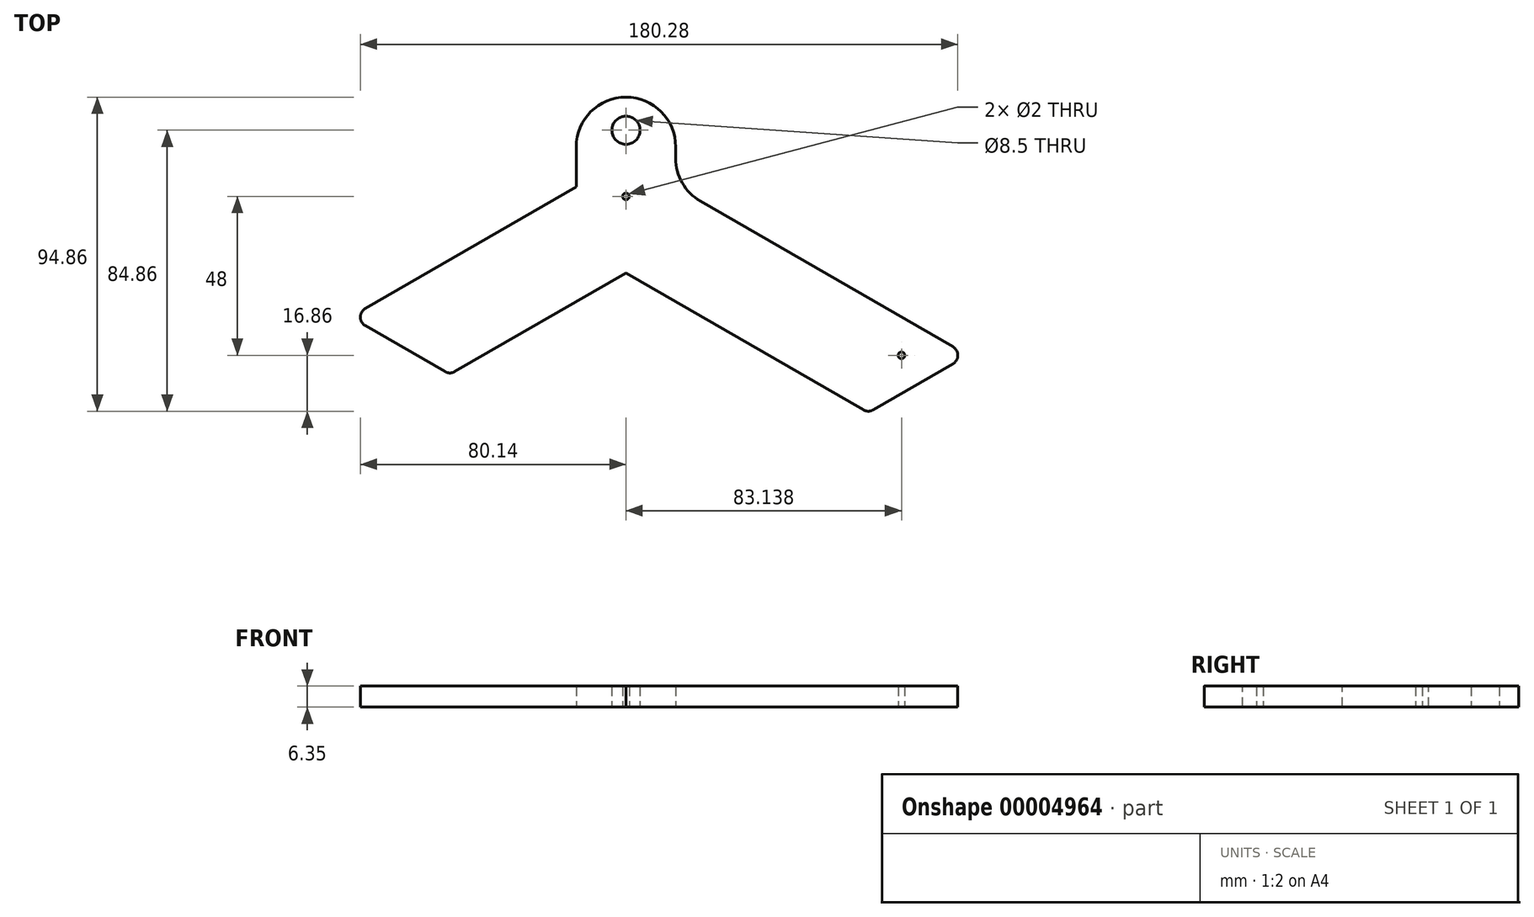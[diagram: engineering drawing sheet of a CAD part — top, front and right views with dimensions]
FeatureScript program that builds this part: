
annotation { "Feature Type Name" : "Feature", "Feature Type Description" : "" }
export const myFeature = defineFeature(function(context is Context, id is Id, definition is map)
    precondition{}
    {
        {
            var Q0;
            Q0=qCreatedBy(makeId("Top.planeOp"),FACE);
            var sketch = newSketch(context, id + "F0", { "sketchPlane" : qUnion([Q0])});
            skLineSegment(sketch, "E0", {"start": v(0, 0) * mm, "end": v(0, 96) * mm, "construction": true});
            skLineSegment(sketch, "E1", {"start": v(0, 96) * mm, "end": v(83.14, 48) * mm, "construction": true});
            skLineSegment(sketch, "E2", {"start": v(83.14, 48) * mm, "end": v(0, 0) * mm, "construction": true});
            skCircle(sketch, "E3", {"center": v(0, 96) * mm, "radius": 1 * mm});
            skCircle(sketch, "E4", {"center": v(83.14, 48) * mm, "radius": 1 * mm});
            skLineSegment(sketch, "E5", {"start": v(0, 96) * mm, "end": v(0, 116) * mm, "construction": true});
            skCircle(sketch, "E6", {"center": v(0, 116) * mm, "radius": 4.25 * mm});
            skLineSegment(sketch, "E7", {"start": v(-15, 81.57) * mm, "end": v(73.14, 30.68) * mm});
            skLineSegment(sketch, "E8", {"start": v(73.14, 30.68) * mm, "end": v(103.14, 48) * mm});
            skLineSegment(sketch, "E9", {"start": v(103.14, 48) * mm, "end": v(15, 98.89) * mm});
            skLineSegment(sketch, "E10", {"start": v(-15, 81.57) * mm, "end": v(-15, 126) * mm});
            skLineSegment(sketch, "E11", {"start": v(15, 98.89) * mm, "end": v(15, 126) * mm});
            skLineSegment(sketch, "E12", {"start": v(15, 126) * mm, "end": v(-15, 126) * mm});
            skLineSegment(sketch, "E13", {"start": v(0, 116) * mm, "end": v(0, 126) * mm, "construction": true});
            skLineSegment(sketch, "E14.1.0", {"start": v(-116.62, -50) * mm, "end": v(-101.62, -76) * mm, "construction": true});
            skLineSegment(sketch, "E14.1.1", {"start": v(-63.14, -53.77) * mm, "end": v(-101.62, -76) * mm, "construction": true});
            skLineSegment(sketch, "E14.1.2", {"start": v(-93.14, -36.45) * mm, "end": v(-116.62, -50) * mm, "construction": true});
            skLineSegment(sketch, "E14.1.3", {"start": v(-93.14, 65.32) * mm, "end": v(-93.14, -36.45) * mm, "construction": true});
            skLineSegment(sketch, "E14.1.4", {"start": v(-63.14, 48) * mm, "end": v(-93.14, 65.32) * mm, "construction": true});
            skLineSegment(sketch, "E14.1.5", {"start": v(-63.14, -53.77) * mm, "end": v(-63.14, 48) * mm, "construction": true});
            skLineSegment(sketch, "E14.2.0", {"start": v(101.62, -76) * mm, "end": v(116.62, -50) * mm, "construction": true});
            skLineSegment(sketch, "E14.2.1", {"start": v(78.14, -27.8) * mm, "end": v(116.62, -50) * mm, "construction": true});
            skLineSegment(sketch, "E14.2.2", {"start": v(78.14, -62.43) * mm, "end": v(101.62, -76) * mm, "construction": true});
            skLineSegment(sketch, "E14.2.3", {"start": v(-10, -113.32) * mm, "end": v(78.14, -62.43) * mm, "construction": true});
            skLineSegment(sketch, "E14.2.4", {"start": v(-10, -78.68) * mm, "end": v(-10, -113.32) * mm, "construction": true});
            skLineSegment(sketch, "E14.2.5", {"start": v(78.14, -27.8) * mm, "end": v(-10, -78.68) * mm, "construction": true});
            skPoint(sketch, "E14.center", {"position": v(0, 0) * mm});
            skSolve(sketch);
        }
        {
            var Q0;
            Q0 = qSketchRegion(id + "F0", true);
            extrude(context, id + "F1", {"entities" : qUnion([Q0]), "depth" : 6.35 * mm});
        }
        {
            var Q0;
            Q0=makeQuery(id+"F1.opExtrude","CAP_FACE",FACE,{"disambiguationData":[OSD([sQuery(id+"F0.wireOp",EDGE,"E3"),sQuery(id+"F0.wireOp",EDGE,"E4"),sQuery(id+"F0.wireOp",EDGE,"E6"),sQuery(id+"F0.wireOp",EDGE,"E7"),sQuery(id+"F0.wireOp",EDGE,"E8"),sQuery(id+"F0.wireOp",EDGE,"E9"),sQuery(id+"F0.wireOp",EDGE,"E10"),sQuery(id+"F0.wireOp",EDGE,"E11"),sQuery(id+"F0.wireOp",EDGE,"E12")])],"isStart":false});
            var sketch = newSketch(context, id + "F2", { "sketchPlane" : qUnion([Q0])});
            skLineSegment(sketch, "E15", {"start": v(0, 0) * mm, "end": v(-83.14, 48) * mm, "construction": true});
            skLineSegment(sketch, "E16", {"start": v(0, 0) * mm, "end": v(0, 96) * mm, "construction": true});
            skLineSegment(sketch, "E17", {"start": v(0, 96) * mm, "end": v(-83.14, 48) * mm, "construction": true});
            skLineSegment(sketch, "E18", {"start": v(-15, 98.89) * mm, "end": v(-83.14, 59.55) * mm});
            skLineSegment(sketch, "E19", {"start": v(-93.14, 53.77) * mm, "end": v(-63.14, 36.45) * mm, "construction": true});
            skLineSegment(sketch, "E20", {"start": v(-53.14, 42.23) * mm, "end": v(0, 72.9) * mm});
            skLineSegment(sketch, "E21.0", {"start": v(-15, 81.57) * mm, "end": v(-15, 98.89) * mm});
            skLineSegment(sketch, "E21.1", {"start": v(-15, 81.57) * mm, "end": v(0, 72.9) * mm});
            skPoint(sketch, "E22.orphan", {"position": v(-15, 126) * mm});
            skPoint(sketch, "E23.orphan", {"position": v(73.14, 30.68) * mm});
            skLineSegment(sketch, "E24", {"start": v(-83.14, 59.55) * mm, "end": v(-53.14, 42.23) * mm});
            skSolve(sketch);
        }
        {
            var Q0;
            Q0 = qSketchRegion(id + "F2", true);
            var Q1;
            Q1=makeQuery(id+"F1.opExtrude","CAP_FACE",FACE,{"disambiguationData":[OSD([sQuery(id+"F0.wireOp",EDGE,"E3"),sQuery(id+"F0.wireOp",EDGE,"E4"),sQuery(id+"F0.wireOp",EDGE,"E6"),sQuery(id+"F0.wireOp",EDGE,"E7"),sQuery(id+"F0.wireOp",EDGE,"E8"),sQuery(id+"F0.wireOp",EDGE,"E9"),sQuery(id+"F0.wireOp",EDGE,"E10"),sQuery(id+"F0.wireOp",EDGE,"E11"),sQuery(id+"F0.wireOp",EDGE,"E12")])],"isStart":true});
            extrude(context, id + "F3", {"entities" : qUnion([Q0]), "operationType" : NewBodyOperationType.ADD, "endBound" : BoundingType.UP_TO_SURFACE, "oppositeDirection" : true, "endBoundEntityFace" : qUnion([Q1]), "depth" : 25 * mm});
        }
        {
            var Q0;
            Q0=makeQuery(id+"F1.opExtrude","SWEPT_EDGE",EDGE,{"disambiguationData":[OSD([sQuery(id+"F0.wireOp",EDGE,"E11"),sQuery(id+"F0.wireOp",EDGE,"E12")])]});
            var Q1;
            Q1=makeQuery(id+"F1.opExtrude","SWEPT_EDGE",EDGE,{"disambiguationData":[OSD([sQuery(id+"F0.wireOp",EDGE,"E10"),sQuery(id+"F0.wireOp",EDGE,"E12")])]});
            var Q2;
            Q2=makeQuery(id+"F1.opExtrude","SWEPT_EDGE",EDGE,{"disambiguationData":[OSD([sQuery(id+"F0.wireOp",EDGE,"E9"),sQuery(id+"F0.wireOp",EDGE,"E11")])]});
            var Q3;
            Q3=makeQuery(id+"F1.opExtrude","SWEPT_EDGE",EDGE,{"disambiguationData":[OSD([sQuery(id+"F0.wireOp",EDGE,"E7"),sQuery(id+"F0.wireOp",EDGE,"E10")])]});
            var Q4;
            Q4=makeQuery(id+"F3.opExtrude","SWEPT_EDGE",EDGE,{"disambiguationData":[OSD([sQuery(id+"F0.wireOp",EDGE,"E10"),sQuery(id+"F2.wireOp",EDGE,"E18"),sQuery(id+"F2.wireOp",EDGE,"E21.0")])]});
            var Q5;
            Q5=makeQuery(id+"F3.opExtrude","SWEPT_EDGE",EDGE,{"disambiguationData":[OSD([sQuery(id+"F0.wireOp",EDGE,"E7"),sQuery(id+"F2.wireOp",EDGE,"E20"),sQuery(id+"F2.wireOp",EDGE,"E21.1")])]});
            fillet(context, id + "F4", {"entities" : qUnion([Q0, Q1, Q2, Q3, Q4, Q5]), "radius" : 15 * mm, "tangentPropagation" : true, "allowEdgeOverflow" : false});
        }
        {
            var Q0;
            Q0=makeQuery(id+"F1.opExtrude","SWEPT_EDGE",EDGE,{"disambiguationData":[OSD([sQuery(id+"F0.wireOp",EDGE,"E8"),sQuery(id+"F0.wireOp",EDGE,"E9")])]});
            var Q1;
            Q1=makeQuery(id+"F3.opExtrude","SWEPT_EDGE",EDGE,{"disambiguationData":[OSD([sQuery(id+"F2.wireOp",EDGE,"E18"),sQuery(id+"F2.wireOp",EDGE,"E24")])]});
            var Q2;
            Q2=makeQuery(id+"F3.opExtrude","SWEPT_EDGE",EDGE,{"disambiguationData":[OSD([sQuery(id+"F2.wireOp",EDGE,"E20"),sQuery(id+"F2.wireOp",EDGE,"E24")])]});
            var Q3;
            Q3=makeQuery(id+"F1.opExtrude","SWEPT_EDGE",EDGE,{"disambiguationData":[OSD([sQuery(id+"F0.wireOp",EDGE,"E7"),sQuery(id+"F0.wireOp",EDGE,"E8")])]});
            fillet(context, id + "F5", {"entities" : qUnion([Q0, Q1, Q2, Q3]), "radius" : 3 * mm, "tangentPropagation" : true, "allowEdgeOverflow" : false});
        }
    });
